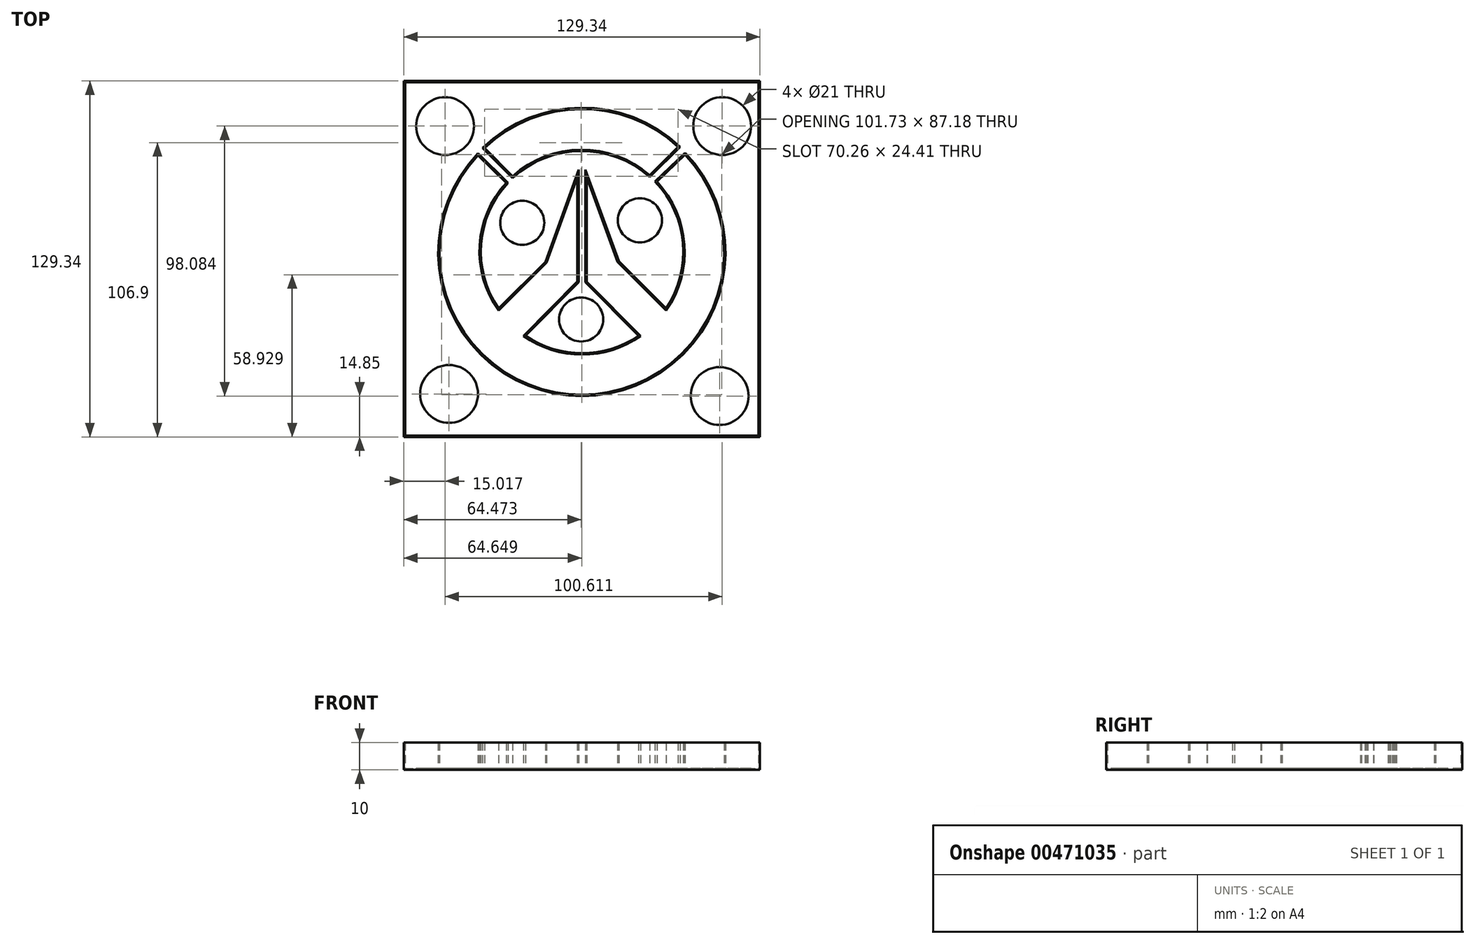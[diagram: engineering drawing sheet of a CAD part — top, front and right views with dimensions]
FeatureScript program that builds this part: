
annotation { "Feature Type Name" : "Feature", "Feature Type Description" : "" }
export const myFeature = defineFeature(function(context is Context, id is Id, definition is map)
    precondition{}
    {
        {
            var Q0;
            Q0=qCreatedBy(makeId("Top.planeOp"),FACE);
            var sketch = newSketch(context, id + "F0", { "sketchPlane" : qUnion([Q0])});
            skArc(sketch, "E0", {"start": v(-37.42, 29.12) * mm, "mid": v(0.36, -57.88) * mm, "end": v(37.73, 29.3) * mm});
            skLineSegment(sketch, "E1", {"start": v(-37.42, 29.12) * mm, "end": v(-27.22, 19.1) * mm});
            skArc(sketch, "E2", {"start": v(-27.22, 19.1) * mm, "mid": v(-36.86, -3.6) * mm, "end": v(-30.02, -27.3) * mm});
            skLineSegment(sketch, "E3", {"start": v(-30.02, -27.3) * mm, "end": v(-12.58, -9.86) * mm});
            skLineSegment(sketch, "E4", {"start": v(-12.58, -9.86) * mm, "end": v(-1.36, 21.07) * mm});
            skLineSegment(sketch, "E5", {"start": v(-1.36, 21.07) * mm, "end": v(-1.36, -16.78) * mm});
            skLineSegment(sketch, "E6", {"start": v(-1.36, -16.78) * mm, "end": v(-20.94, -36.56) * mm});
            skArc(sketch, "E7", {"start": v(-20.94, -36.56) * mm, "mid": v(0.33, -43.31) * mm, "end": v(21.6, -36.56) * mm});
            skLineSegment(sketch, "E8", {"start": v(21.6, -36.56) * mm, "end": v(2, -16.85) * mm});
            skLineSegment(sketch, "E9", {"start": v(2, -16.85) * mm, "end": v(2, 21.07) * mm});
            skLineSegment(sketch, "E10", {"start": v(2, 21.07) * mm, "end": v(13.23, -9.6) * mm});
            skLineSegment(sketch, "E11", {"start": v(13.23, -9.6) * mm, "end": v(30.88, -27.35) * mm});
            skArc(sketch, "E12", {"start": v(30.88, -27.35) * mm, "mid": v(37.46, -3.3) * mm, "end": v(27.49, 19.55) * mm});
            skLineSegment(sketch, "E13", {"start": v(27.49, 19.55) * mm, "end": v(37.73, 29.3) * mm});
            skArc(sketch, "E14", {"start": v(35.17, 32.19) * mm, "mid": v(-0.05, 45.89) * mm, "end": v(-35.09, 31.72) * mm});
            skLineSegment(sketch, "E15", {"start": v(-35.09, 31.72) * mm, "end": v(-24.92, 21.47) * mm});
            skLineSegment(sketch, "E16", {"start": v(35.17, 32.19) * mm, "end": v(24.9, 21.86) * mm});
            skArc(sketch, "E17", {"start": v(24.9, 21.86) * mm, "mid": v(-0.08, 31.16) * mm, "end": v(-24.92, 21.47) * mm});
            skLineSegment(sketch, "E18.bottom", {"start": v(-220.58, 77.85) * mm, "end": v(-91.24, 77.85) * mm});
            skLineSegment(sketch, "E18.top", {"start": v(-220.58, -51.49) * mm, "end": v(-91.24, -51.49) * mm});
            skLineSegment(sketch, "E18.left", {"start": v(-220.58, 77.85) * mm, "end": v(-220.58, -51.49) * mm});
            skLineSegment(sketch, "E18.right", {"start": v(-91.24, 77.85) * mm, "end": v(-91.24, -51.49) * mm});
            skLineSegment(sketch, "E19.bottom", {"start": v(-64.43, 56.12) * mm, "end": v(64.9, 56.12) * mm});
            skLineSegment(sketch, "E19.top", {"start": v(-64.43, -73.22) * mm, "end": v(64.9, -73.22) * mm});
            skLineSegment(sketch, "E19.left", {"start": v(-64.43, 56.12) * mm, "end": v(-64.43, -73.22) * mm});
            skLineSegment(sketch, "E19.right", {"start": v(64.9, 56.12) * mm, "end": v(64.9, -73.22) * mm});
            skCircle(sketch, "E20", {"center": v(-47.96, -57.6) * mm, "radius": 10 * mm});
            skCircle(sketch, "E21", {"center": v(50.28, -58.37) * mm, "radius": 10 * mm});
            skCircle(sketch, "E22", {"center": v(-49.41, 39.71) * mm, "radius": 10 * mm});
            skCircle(sketch, "E23", {"center": v(51.2, 39.71) * mm, "radius": 10 * mm});
            skCircle(sketch, "E24", {"center": v(0, -30.56) * mm, "radius": 7.5 * mm});
            skCircle(sketch, "E25", {"center": v(-21.39, 4.57) * mm, "radius": 7.5 * mm});
            skCircle(sketch, "E26", {"center": v(21.34, 5.49) * mm, "radius": 7.5 * mm});
            skSolve(sketch);
        }
        {
            var Q0;
            Q0=makeQuery(id+"F0.imprint","IMPRINT",FACE,{"disambiguationData":[TD([[makeQuery(id+"F0.imprint","IMPRINT",EDGE,{"derivedFrom":sQuery(id+"F0.wireOp",EDGE,"E0")}),-1.0]])]});
            extrude(context, id + "F1", {"entities" : qUnion([Q0]), "depth" : 10 * mm});
        }
        {
            var Q0;
            Q0=makeQuery(id+"F1.opExtrude","CAP_FACE",FACE,{"disambiguationData":[OSD([sQuery(id+"F0.wireOp",EDGE,"E0"),sQuery(id+"F0.wireOp",EDGE,"E1"),sQuery(id+"F0.wireOp",EDGE,"E2"),sQuery(id+"F0.wireOp",EDGE,"E3"),sQuery(id+"F0.wireOp",EDGE,"E4"),sQuery(id+"F0.wireOp",EDGE,"E5"),sQuery(id+"F0.wireOp",EDGE,"E6"),sQuery(id+"F0.wireOp",EDGE,"E7"),sQuery(id+"F0.wireOp",EDGE,"E8"),sQuery(id+"F0.wireOp",EDGE,"E9"),sQuery(id+"F0.wireOp",EDGE,"E10"),sQuery(id+"F0.wireOp",EDGE,"E11"),sQuery(id+"F0.wireOp",EDGE,"E12"),sQuery(id+"F0.wireOp",EDGE,"E13"),sQuery(id+"F0.wireOp",EDGE,"E14"),sQuery(id+"F0.wireOp",EDGE,"E15"),sQuery(id+"F0.wireOp",EDGE,"E16"),sQuery(id+"F0.wireOp",EDGE,"E17"),sQuery(id+"F0.wireOp",EDGE,"E19.bottom"),sQuery(id+"F0.wireOp",EDGE,"E19.top"),sQuery(id+"F0.wireOp",EDGE,"E19.left"),sQuery(id+"F0.wireOp",EDGE,"E19.right")])],"isStart":false});
            shell(context, id + "F2", {"entities" : qUnion([Q0]), "thickness" : 0.5 * mm});
        }
        {
            var Q0;
            {var subQ0=sQuery(id+"F0.wireOp",EDGE,"E20");var subQ1=sQuery(id+"F0.wireOp",EDGE,"E19.right");var subQ2=sQuery(id+"F0.wireOp",EDGE,"E19.left");var subQ3=sQuery(id+"F0.wireOp",EDGE,"E19.top");var subQ4=sQuery(id+"F0.wireOp",EDGE,"E19.bottom");var subQ5=sQuery(id+"F0.wireOp",EDGE,"E17");var subQ6=sQuery(id+"F0.wireOp",EDGE,"E16");var subQ7=sQuery(id+"F0.wireOp",EDGE,"E15");var subQ8=sQuery(id+"F0.wireOp",EDGE,"E14");var subQ9=sQuery(id+"F0.wireOp",EDGE,"E13");var subQ10=sQuery(id+"F0.wireOp",EDGE,"E12");var subQ11=sQuery(id+"F0.wireOp",EDGE,"E11");var subQ12=sQuery(id+"F0.wireOp",EDGE,"E10");var subQ13=sQuery(id+"F0.wireOp",EDGE,"E9");var subQ14=sQuery(id+"F0.wireOp",EDGE,"E8");var subQ15=sQuery(id+"F0.wireOp",EDGE,"E7");var subQ16=sQuery(id+"F0.wireOp",EDGE,"E6");var subQ17=sQuery(id+"F0.wireOp",EDGE,"E5");var subQ18=sQuery(id+"F0.wireOp",EDGE,"E4");var subQ19=sQuery(id+"F0.wireOp",EDGE,"E3");var subQ20=sQuery(id+"F0.wireOp",EDGE,"E2");var subQ21=sQuery(id+"F0.wireOp",EDGE,"E1");var subQ22=sQuery(id+"F0.wireOp",EDGE,"E0");Q0=makeQuery(id+"F2.opShell","OFFSET_FACE",FACE,{"disambiguationData":[OSD([subQ22,subQ21,subQ20,subQ19,subQ18,subQ17,subQ16,subQ15,subQ14,subQ13,subQ12,subQ11,subQ10,subQ9,subQ8,subQ7,subQ6,subQ5,subQ4,subQ3,subQ2,subQ1,subQ0]),TDD([makeQuery(id+"F1.opExtrude","CAP_FACE",FACE,{"disambiguationData":[OSD([subQ22,subQ21,subQ20,subQ19,subQ18,subQ17,subQ16,subQ15,subQ14,subQ13,subQ12,subQ11,subQ10,subQ9,subQ8,subQ7,subQ6,subQ5,subQ4,subQ3,subQ2,subQ1,subQ0])],"isStart":false})]),OD(2.0)]});}
            var Q1;
            {var subQ0=sQuery(id+"F0.wireOp",EDGE,"E26");var subQ1=sQuery(id+"F0.wireOp",EDGE,"E25");var subQ2=sQuery(id+"F0.wireOp",EDGE,"E24");var subQ3=sQuery(id+"F0.wireOp",EDGE,"E23");var subQ4=sQuery(id+"F0.wireOp",EDGE,"E22");var subQ5=sQuery(id+"F0.wireOp",EDGE,"E21");var subQ6=sQuery(id+"F0.wireOp",EDGE,"E20");var subQ7=sQuery(id+"F0.wireOp",EDGE,"E19.right");var subQ8=sQuery(id+"F0.wireOp",EDGE,"E19.left");var subQ9=sQuery(id+"F0.wireOp",EDGE,"E19.top");var subQ10=sQuery(id+"F0.wireOp",EDGE,"E19.bottom");var subQ11=sQuery(id+"F0.wireOp",EDGE,"E17");var subQ12=sQuery(id+"F0.wireOp",EDGE,"E16");var subQ13=sQuery(id+"F0.wireOp",EDGE,"E15");var subQ14=sQuery(id+"F0.wireOp",EDGE,"E14");var subQ15=sQuery(id+"F0.wireOp",EDGE,"E13");var subQ16=sQuery(id+"F0.wireOp",EDGE,"E12");var subQ17=sQuery(id+"F0.wireOp",EDGE,"E11");var subQ18=sQuery(id+"F0.wireOp",EDGE,"E10");var subQ19=sQuery(id+"F0.wireOp",EDGE,"E9");var subQ20=sQuery(id+"F0.wireOp",EDGE,"E8");var subQ21=sQuery(id+"F0.wireOp",EDGE,"E7");var subQ22=sQuery(id+"F0.wireOp",EDGE,"E6");var subQ23=sQuery(id+"F0.wireOp",EDGE,"E5");var subQ24=sQuery(id+"F0.wireOp",EDGE,"E4");var subQ25=sQuery(id+"F0.wireOp",EDGE,"E3");var subQ26=sQuery(id+"F0.wireOp",EDGE,"E2");var subQ27=sQuery(id+"F0.wireOp",EDGE,"E1");var subQ28=sQuery(id+"F0.wireOp",EDGE,"E0");Q1=makeQuery(id+"F2.opShell","OFFSET_FACE",FACE,{"disambiguationData":[OSD([subQ28,subQ27,subQ26,subQ25,subQ24,subQ23,subQ22,subQ21,subQ20,subQ19,subQ18,subQ17,subQ16,subQ15,subQ14,subQ13,subQ12,subQ11,subQ10,subQ9,subQ8,subQ7,subQ6,subQ5,subQ4,subQ3,subQ2,subQ1,subQ0]),TDD([makeQuery(id+"F1.opExtrude","CAP_FACE",FACE,{"disambiguationData":[OSD([subQ28,subQ27,subQ26,subQ25,subQ24,subQ23,subQ22,subQ21,subQ20,subQ19,subQ18,subQ17,subQ16,subQ15,subQ14,subQ13,subQ12,subQ11,subQ10,subQ9,subQ8,subQ7,subQ6,subQ5,subQ4,subQ3,subQ2,subQ1,subQ0])],"isStart":false})]),OD(4.0)]});}
            var Q2;
            {var subQ0=sQuery(id+"F0.wireOp",EDGE,"E26");var subQ1=sQuery(id+"F0.wireOp",EDGE,"E25");var subQ2=sQuery(id+"F0.wireOp",EDGE,"E24");var subQ3=sQuery(id+"F0.wireOp",EDGE,"E23");var subQ4=sQuery(id+"F0.wireOp",EDGE,"E22");var subQ5=sQuery(id+"F0.wireOp",EDGE,"E21");var subQ6=sQuery(id+"F0.wireOp",EDGE,"E20");var subQ7=sQuery(id+"F0.wireOp",EDGE,"E19.right");var subQ8=sQuery(id+"F0.wireOp",EDGE,"E19.left");var subQ9=sQuery(id+"F0.wireOp",EDGE,"E19.top");var subQ10=sQuery(id+"F0.wireOp",EDGE,"E19.bottom");var subQ11=sQuery(id+"F0.wireOp",EDGE,"E17");var subQ12=sQuery(id+"F0.wireOp",EDGE,"E16");var subQ13=sQuery(id+"F0.wireOp",EDGE,"E15");var subQ14=sQuery(id+"F0.wireOp",EDGE,"E14");var subQ15=sQuery(id+"F0.wireOp",EDGE,"E13");var subQ16=sQuery(id+"F0.wireOp",EDGE,"E12");var subQ17=sQuery(id+"F0.wireOp",EDGE,"E11");var subQ18=sQuery(id+"F0.wireOp",EDGE,"E10");var subQ19=sQuery(id+"F0.wireOp",EDGE,"E9");var subQ20=sQuery(id+"F0.wireOp",EDGE,"E8");var subQ21=sQuery(id+"F0.wireOp",EDGE,"E7");var subQ22=sQuery(id+"F0.wireOp",EDGE,"E6");var subQ23=sQuery(id+"F0.wireOp",EDGE,"E5");var subQ24=sQuery(id+"F0.wireOp",EDGE,"E4");var subQ25=sQuery(id+"F0.wireOp",EDGE,"E3");var subQ26=sQuery(id+"F0.wireOp",EDGE,"E2");var subQ27=sQuery(id+"F0.wireOp",EDGE,"E1");var subQ28=sQuery(id+"F0.wireOp",EDGE,"E0");Q2=makeQuery(id+"F2.opShell","OFFSET_FACE",FACE,{"disambiguationData":[OSD([subQ28,subQ27,subQ26,subQ25,subQ24,subQ23,subQ22,subQ21,subQ20,subQ19,subQ18,subQ17,subQ16,subQ15,subQ14,subQ13,subQ12,subQ11,subQ10,subQ9,subQ8,subQ7,subQ6,subQ5,subQ4,subQ3,subQ2,subQ1,subQ0]),TDD([makeQuery(id+"F1.opExtrude","CAP_FACE",FACE,{"disambiguationData":[OSD([subQ28,subQ27,subQ26,subQ25,subQ24,subQ23,subQ22,subQ21,subQ20,subQ19,subQ18,subQ17,subQ16,subQ15,subQ14,subQ13,subQ12,subQ11,subQ10,subQ9,subQ8,subQ7,subQ6,subQ5,subQ4,subQ3,subQ2,subQ1,subQ0])],"isStart":false})]),OD(5.0)]});}
            var Q3;
            {var subQ0=sQuery(id+"F0.wireOp",EDGE,"E26");var subQ1=sQuery(id+"F0.wireOp",EDGE,"E25");var subQ2=sQuery(id+"F0.wireOp",EDGE,"E24");var subQ3=sQuery(id+"F0.wireOp",EDGE,"E23");var subQ4=sQuery(id+"F0.wireOp",EDGE,"E22");var subQ5=sQuery(id+"F0.wireOp",EDGE,"E21");var subQ6=sQuery(id+"F0.wireOp",EDGE,"E20");var subQ7=sQuery(id+"F0.wireOp",EDGE,"E19.right");var subQ8=sQuery(id+"F0.wireOp",EDGE,"E19.left");var subQ9=sQuery(id+"F0.wireOp",EDGE,"E19.top");var subQ10=sQuery(id+"F0.wireOp",EDGE,"E19.bottom");var subQ11=sQuery(id+"F0.wireOp",EDGE,"E17");var subQ12=sQuery(id+"F0.wireOp",EDGE,"E16");var subQ13=sQuery(id+"F0.wireOp",EDGE,"E15");var subQ14=sQuery(id+"F0.wireOp",EDGE,"E14");var subQ15=sQuery(id+"F0.wireOp",EDGE,"E13");var subQ16=sQuery(id+"F0.wireOp",EDGE,"E12");var subQ17=sQuery(id+"F0.wireOp",EDGE,"E11");var subQ18=sQuery(id+"F0.wireOp",EDGE,"E10");var subQ19=sQuery(id+"F0.wireOp",EDGE,"E9");var subQ20=sQuery(id+"F0.wireOp",EDGE,"E8");var subQ21=sQuery(id+"F0.wireOp",EDGE,"E7");var subQ22=sQuery(id+"F0.wireOp",EDGE,"E6");var subQ23=sQuery(id+"F0.wireOp",EDGE,"E5");var subQ24=sQuery(id+"F0.wireOp",EDGE,"E4");var subQ25=sQuery(id+"F0.wireOp",EDGE,"E3");var subQ26=sQuery(id+"F0.wireOp",EDGE,"E2");var subQ27=sQuery(id+"F0.wireOp",EDGE,"E1");var subQ28=sQuery(id+"F0.wireOp",EDGE,"E0");Q3=makeQuery(id+"F2.opShell","OFFSET_FACE",FACE,{"disambiguationData":[OSD([subQ28,subQ27,subQ26,subQ25,subQ24,subQ23,subQ22,subQ21,subQ20,subQ19,subQ18,subQ17,subQ16,subQ15,subQ14,subQ13,subQ12,subQ11,subQ10,subQ9,subQ8,subQ7,subQ6,subQ5,subQ4,subQ3,subQ2,subQ1,subQ0]),TDD([makeQuery(id+"F1.opExtrude","CAP_FACE",FACE,{"disambiguationData":[OSD([subQ28,subQ27,subQ26,subQ25,subQ24,subQ23,subQ22,subQ21,subQ20,subQ19,subQ18,subQ17,subQ16,subQ15,subQ14,subQ13,subQ12,subQ11,subQ10,subQ9,subQ8,subQ7,subQ6,subQ5,subQ4,subQ3,subQ2,subQ1,subQ0])],"isStart":false})]),OD(3.0)]});}
            var Q4;
            {var subQ0=sQuery(id+"F0.wireOp",EDGE,"E26");var subQ1=sQuery(id+"F0.wireOp",EDGE,"E25");var subQ2=sQuery(id+"F0.wireOp",EDGE,"E24");var subQ3=sQuery(id+"F0.wireOp",EDGE,"E23");var subQ4=sQuery(id+"F0.wireOp",EDGE,"E22");var subQ5=sQuery(id+"F0.wireOp",EDGE,"E21");var subQ6=sQuery(id+"F0.wireOp",EDGE,"E20");var subQ7=sQuery(id+"F0.wireOp",EDGE,"E19.right");var subQ8=sQuery(id+"F0.wireOp",EDGE,"E19.left");var subQ9=sQuery(id+"F0.wireOp",EDGE,"E19.top");var subQ10=sQuery(id+"F0.wireOp",EDGE,"E19.bottom");var subQ11=sQuery(id+"F0.wireOp",EDGE,"E17");var subQ12=sQuery(id+"F0.wireOp",EDGE,"E16");var subQ13=sQuery(id+"F0.wireOp",EDGE,"E15");var subQ14=sQuery(id+"F0.wireOp",EDGE,"E14");var subQ15=sQuery(id+"F0.wireOp",EDGE,"E13");var subQ16=sQuery(id+"F0.wireOp",EDGE,"E12");var subQ17=sQuery(id+"F0.wireOp",EDGE,"E11");var subQ18=sQuery(id+"F0.wireOp",EDGE,"E10");var subQ19=sQuery(id+"F0.wireOp",EDGE,"E9");var subQ20=sQuery(id+"F0.wireOp",EDGE,"E8");var subQ21=sQuery(id+"F0.wireOp",EDGE,"E7");var subQ22=sQuery(id+"F0.wireOp",EDGE,"E6");var subQ23=sQuery(id+"F0.wireOp",EDGE,"E5");var subQ24=sQuery(id+"F0.wireOp",EDGE,"E4");var subQ25=sQuery(id+"F0.wireOp",EDGE,"E3");var subQ26=sQuery(id+"F0.wireOp",EDGE,"E2");var subQ27=sQuery(id+"F0.wireOp",EDGE,"E1");var subQ28=sQuery(id+"F0.wireOp",EDGE,"E0");Q4=makeQuery(id+"F2.opShell","OFFSET_FACE",FACE,{"disambiguationData":[OSD([subQ28,subQ27,subQ26,subQ25,subQ24,subQ23,subQ22,subQ21,subQ20,subQ19,subQ18,subQ17,subQ16,subQ15,subQ14,subQ13,subQ12,subQ11,subQ10,subQ9,subQ8,subQ7,subQ6,subQ5,subQ4,subQ3,subQ2,subQ1,subQ0]),TDD([makeQuery(id+"F1.opExtrude","CAP_FACE",FACE,{"disambiguationData":[OSD([subQ28,subQ27,subQ26,subQ25,subQ24,subQ23,subQ22,subQ21,subQ20,subQ19,subQ18,subQ17,subQ16,subQ15,subQ14,subQ13,subQ12,subQ11,subQ10,subQ9,subQ8,subQ7,subQ6,subQ5,subQ4,subQ3,subQ2,subQ1,subQ0])],"isStart":false})]),OD(6.0)]});}
            var Q5;
            {var subQ0=sQuery(id+"F0.wireOp",EDGE,"E26");var subQ1=sQuery(id+"F0.wireOp",EDGE,"E25");var subQ2=sQuery(id+"F0.wireOp",EDGE,"E24");var subQ3=sQuery(id+"F0.wireOp",EDGE,"E23");var subQ4=sQuery(id+"F0.wireOp",EDGE,"E22");var subQ5=sQuery(id+"F0.wireOp",EDGE,"E21");var subQ6=sQuery(id+"F0.wireOp",EDGE,"E20");var subQ7=sQuery(id+"F0.wireOp",EDGE,"E19.right");var subQ8=sQuery(id+"F0.wireOp",EDGE,"E19.left");var subQ9=sQuery(id+"F0.wireOp",EDGE,"E19.top");var subQ10=sQuery(id+"F0.wireOp",EDGE,"E19.bottom");var subQ11=sQuery(id+"F0.wireOp",EDGE,"E17");var subQ12=sQuery(id+"F0.wireOp",EDGE,"E16");var subQ13=sQuery(id+"F0.wireOp",EDGE,"E15");var subQ14=sQuery(id+"F0.wireOp",EDGE,"E14");var subQ15=sQuery(id+"F0.wireOp",EDGE,"E13");var subQ16=sQuery(id+"F0.wireOp",EDGE,"E12");var subQ17=sQuery(id+"F0.wireOp",EDGE,"E11");var subQ18=sQuery(id+"F0.wireOp",EDGE,"E10");var subQ19=sQuery(id+"F0.wireOp",EDGE,"E9");var subQ20=sQuery(id+"F0.wireOp",EDGE,"E8");var subQ21=sQuery(id+"F0.wireOp",EDGE,"E7");var subQ22=sQuery(id+"F0.wireOp",EDGE,"E6");var subQ23=sQuery(id+"F0.wireOp",EDGE,"E5");var subQ24=sQuery(id+"F0.wireOp",EDGE,"E4");var subQ25=sQuery(id+"F0.wireOp",EDGE,"E3");var subQ26=sQuery(id+"F0.wireOp",EDGE,"E2");var subQ27=sQuery(id+"F0.wireOp",EDGE,"E1");var subQ28=sQuery(id+"F0.wireOp",EDGE,"E0");Q5=makeQuery(id+"F2.opShell","OFFSET_FACE",FACE,{"disambiguationData":[OSD([subQ28,subQ27,subQ26,subQ25,subQ24,subQ23,subQ22,subQ21,subQ20,subQ19,subQ18,subQ17,subQ16,subQ15,subQ14,subQ13,subQ12,subQ11,subQ10,subQ9,subQ8,subQ7,subQ6,subQ5,subQ4,subQ3,subQ2,subQ1,subQ0]),TDD([makeQuery(id+"F1.opExtrude","CAP_FACE",FACE,{"disambiguationData":[OSD([subQ28,subQ27,subQ26,subQ25,subQ24,subQ23,subQ22,subQ21,subQ20,subQ19,subQ18,subQ17,subQ16,subQ15,subQ14,subQ13,subQ12,subQ11,subQ10,subQ9,subQ8,subQ7,subQ6,subQ5,subQ4,subQ3,subQ2,subQ1,subQ0])],"isStart":false})]),OD(7.0)]});}
            var Q6;
            {var subQ0=sQuery(id+"F0.wireOp",EDGE,"E26");var subQ1=sQuery(id+"F0.wireOp",EDGE,"E25");var subQ2=sQuery(id+"F0.wireOp",EDGE,"E24");var subQ3=sQuery(id+"F0.wireOp",EDGE,"E23");var subQ4=sQuery(id+"F0.wireOp",EDGE,"E22");var subQ5=sQuery(id+"F0.wireOp",EDGE,"E21");var subQ6=sQuery(id+"F0.wireOp",EDGE,"E20");var subQ7=sQuery(id+"F0.wireOp",EDGE,"E19.right");var subQ8=sQuery(id+"F0.wireOp",EDGE,"E19.left");var subQ9=sQuery(id+"F0.wireOp",EDGE,"E19.top");var subQ10=sQuery(id+"F0.wireOp",EDGE,"E19.bottom");var subQ11=sQuery(id+"F0.wireOp",EDGE,"E17");var subQ12=sQuery(id+"F0.wireOp",EDGE,"E16");var subQ13=sQuery(id+"F0.wireOp",EDGE,"E15");var subQ14=sQuery(id+"F0.wireOp",EDGE,"E14");var subQ15=sQuery(id+"F0.wireOp",EDGE,"E13");var subQ16=sQuery(id+"F0.wireOp",EDGE,"E12");var subQ17=sQuery(id+"F0.wireOp",EDGE,"E11");var subQ18=sQuery(id+"F0.wireOp",EDGE,"E10");var subQ19=sQuery(id+"F0.wireOp",EDGE,"E9");var subQ20=sQuery(id+"F0.wireOp",EDGE,"E8");var subQ21=sQuery(id+"F0.wireOp",EDGE,"E7");var subQ22=sQuery(id+"F0.wireOp",EDGE,"E6");var subQ23=sQuery(id+"F0.wireOp",EDGE,"E5");var subQ24=sQuery(id+"F0.wireOp",EDGE,"E4");var subQ25=sQuery(id+"F0.wireOp",EDGE,"E3");var subQ26=sQuery(id+"F0.wireOp",EDGE,"E2");var subQ27=sQuery(id+"F0.wireOp",EDGE,"E1");var subQ28=sQuery(id+"F0.wireOp",EDGE,"E0");Q6=makeQuery(id+"F2.opShell","OFFSET_FACE",FACE,{"disambiguationData":[OSD([subQ28,subQ27,subQ26,subQ25,subQ24,subQ23,subQ22,subQ21,subQ20,subQ19,subQ18,subQ17,subQ16,subQ15,subQ14,subQ13,subQ12,subQ11,subQ10,subQ9,subQ8,subQ7,subQ6,subQ5,subQ4,subQ3,subQ2,subQ1,subQ0]),TDD([makeQuery(id+"F1.opExtrude","CAP_FACE",FACE,{"disambiguationData":[OSD([subQ28,subQ27,subQ26,subQ25,subQ24,subQ23,subQ22,subQ21,subQ20,subQ19,subQ18,subQ17,subQ16,subQ15,subQ14,subQ13,subQ12,subQ11,subQ10,subQ9,subQ8,subQ7,subQ6,subQ5,subQ4,subQ3,subQ2,subQ1,subQ0])],"isStart":false})]),OD(8.0)]});}
            extrude(context, id + "F3", {"entities" : qUnion([Q0, Q1, Q2, Q3, Q4, Q5, Q6]), "operationType" : NewBodyOperationType.REMOVE, "oppositeDirection" : true, "depth" : 25 * mm});
        }
    });
